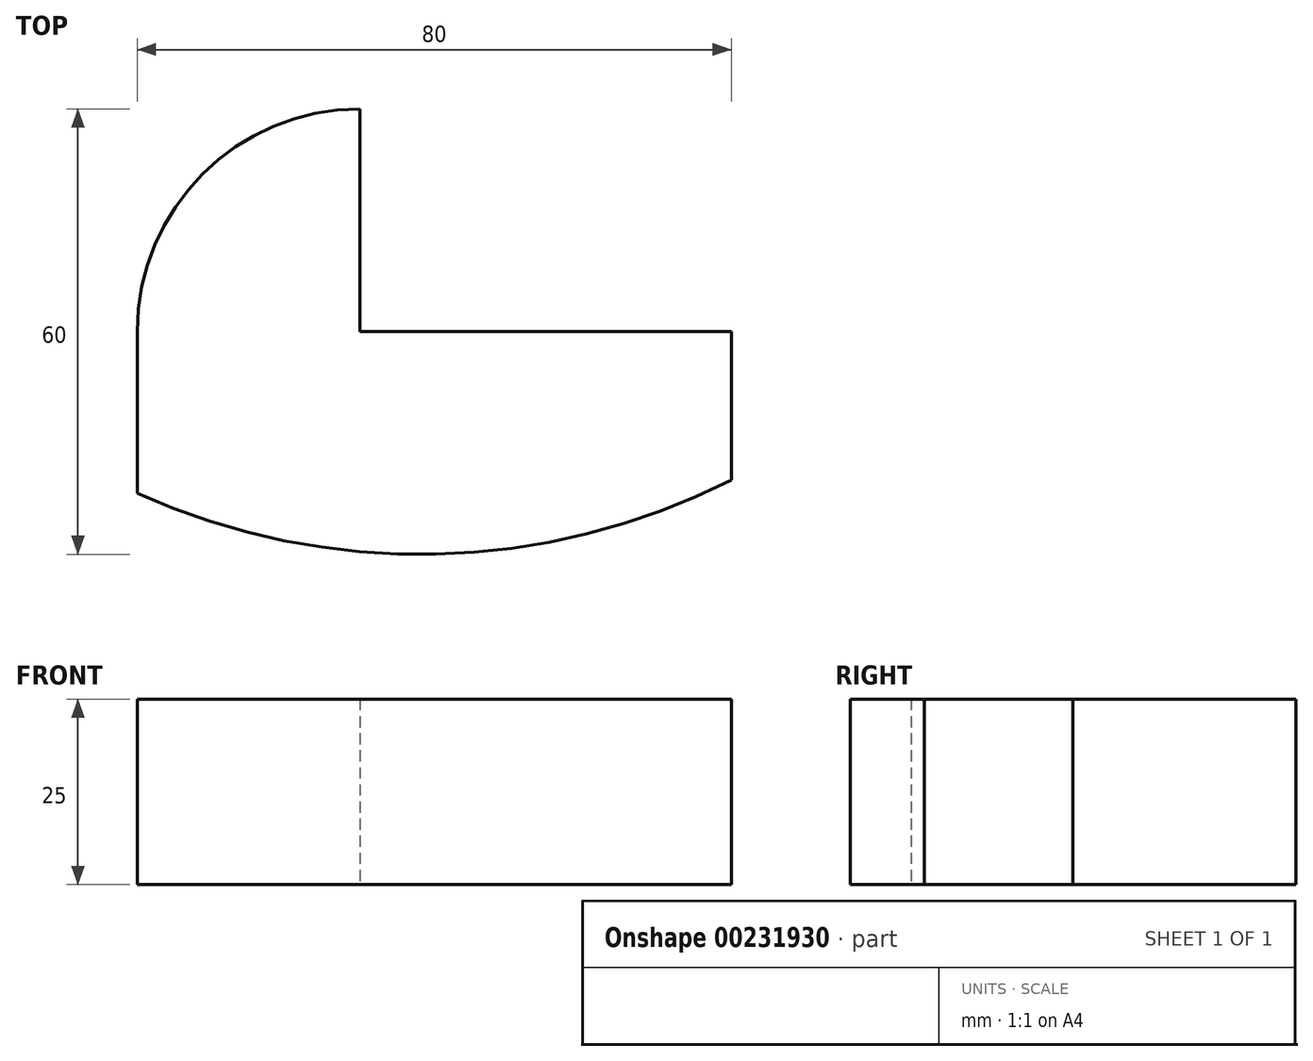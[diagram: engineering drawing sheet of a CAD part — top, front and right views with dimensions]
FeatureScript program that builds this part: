
annotation { "Feature Type Name" : "Feature", "Feature Type Description" : "" }
export const myFeature = defineFeature(function(context is Context, id is Id, definition is map)
    precondition{}
    {
        {
            var Q0;
            Q0=qCreatedBy(makeId("Top.planeOp"),FACE);
            var sketch = newSketch(context, id + "F0", { "sketchPlane" : qUnion([Q0])});
            skLineSegment(sketch, "E0", {"start": v(35.3, 62.2) * mm, "end": v(35.3, 32.2) * mm});
            skLineSegment(sketch, "E1", {"start": v(35.3, 32.2) * mm, "end": v(85.3, 32.2) * mm});
            skLineSegment(sketch, "E2", {"start": v(85.3, 32.2) * mm, "end": v(85.3, 12.2) * mm});
            skArc(sketch, "E3", {"start": v(35.3, 62.2) * mm, "mid": v(14.09, 53.42) * mm, "end": v(5.3, 32.2) * mm});
            skLineSegment(sketch, "E4", {"start": v(5.3, 32.2) * mm, "end": v(5.3, 10.4) * mm});
            skArc(sketch, "E5", {"start": v(5.3, 10.4) * mm, "mid": v(45.5, 2.23) * mm, "end": v(85.3, 12.2) * mm});
            skSolve(sketch);
        }
        {
            var Q0;
            Q0=makeQuery(id+"F0.imprint","IMPRINT",FACE,{"disambiguationData":[TD([[makeQuery(id+"F0.imprint","IMPRINT",EDGE,{"derivedFrom":sQuery(id+"F0.wireOp",EDGE,"E0")}),-1.0]])]});
            extrude(context, id + "F1", {"entities" : qUnion([Q0]), "depth" : 25 * mm});
        }
    });
